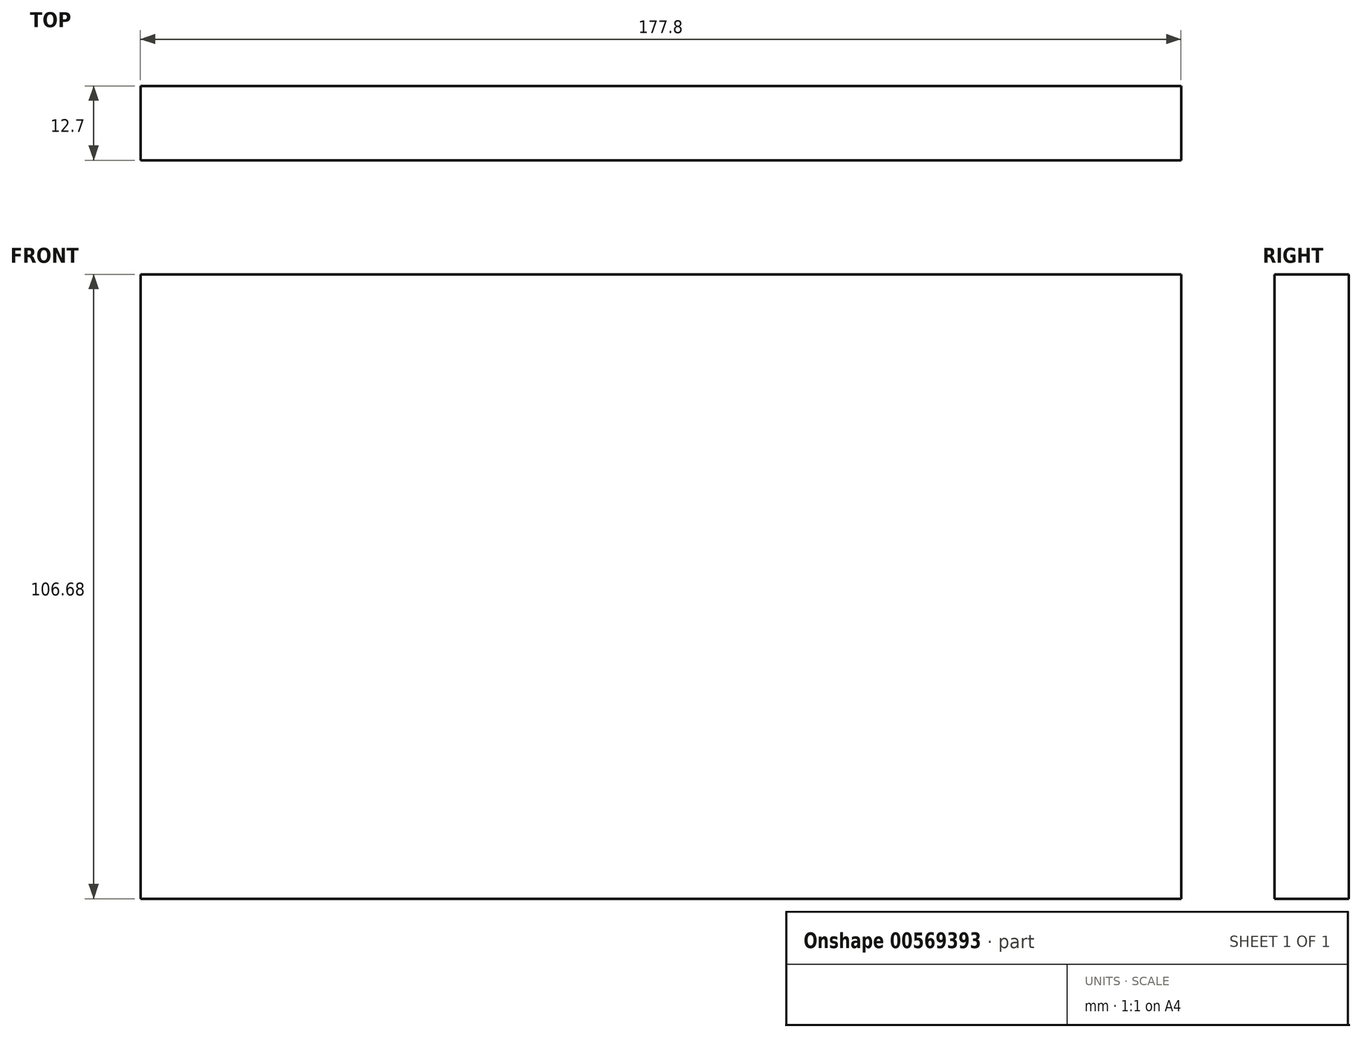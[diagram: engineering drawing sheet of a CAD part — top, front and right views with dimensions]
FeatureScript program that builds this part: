
annotation { "Feature Type Name" : "Feature", "Feature Type Description" : "" }
export const myFeature = defineFeature(function(context is Context, id is Id, definition is map)
    precondition{}
    {
        {
            var Q0;
            Q0=qCreatedBy(makeId("Front.planeOp"),FACE);
            var sketch = newSketch(context, id + "F0", { "sketchPlane" : qUnion([Q0])});
            skLineSegment(sketch, "E0.bottom", {"start": v(-66.08, 48.64) * mm, "end": v(111.72, 48.64) * mm});
            skLineSegment(sketch, "E0.top", {"start": v(-66.08, -58.04) * mm, "end": v(111.72, -58.04) * mm});
            skLineSegment(sketch, "E0.left", {"start": v(-66.08, 48.64) * mm, "end": v(-66.08, -58.04) * mm});
            skLineSegment(sketch, "E0.right", {"start": v(111.72, 48.64) * mm, "end": v(111.72, -58.04) * mm});
            skSolve(sketch);
        }
        {
            var Q0;
            Q0=makeQuery(id+"F0.imprint","IMPRINT",FACE,{"disambiguationData":[TD([[makeQuery(id+"F0.imprint","IMPRINT",EDGE,{"derivedFrom":sQuery(id+"F0.wireOp",EDGE,"E0.bottom")}),-1.0]])]});
            extrude(context, id + "F1", {"entities" : qUnion([Q0]), "endBound" : BoundingType.SYMMETRIC, "depth" : 12.7 * mm, "offsetDistance" : 25.4 * mm});
        }
    });
